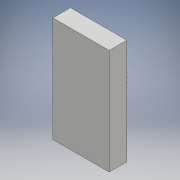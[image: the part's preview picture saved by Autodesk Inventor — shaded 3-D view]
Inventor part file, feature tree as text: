
AUTODESK INVENTOR PART (.ipt)
format: ipt  version: 2018 (Build 220112000, 112)  size: 91,648 bytes
history: native  units: mm
features: sketch x2, extrude x1
ambient origin geometry x8: Origin, YZ Plane, XZ Plane, XY Plane, X Axis, Y Axis, Z Axis, Center Point
bodies: 实体1 (feature_tree)
feature tree (3):
  extrude  "拉伸1"  Depth=16.0mm
  sketch  "草图2"  dims[d2=5.0mm d3=0.0mm]
  sketch  "草图1"  dims[d0=30.0mm d1=16.0mm]
